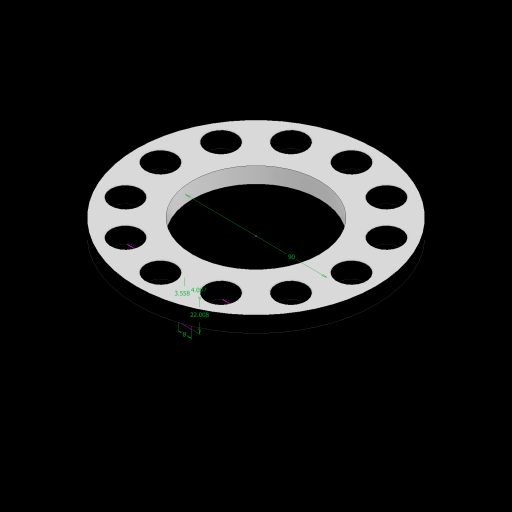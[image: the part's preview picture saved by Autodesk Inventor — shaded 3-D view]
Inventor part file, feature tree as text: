
AUTODESK INVENTOR PART (.ipt)
format: ipt  version: 2023 (Build 270158000, 158)  size: 1,133,056 bytes
history: native  units: mm
features: sketch x10, extrude x9, plane x2, fillet x1, projected_geometry x1
ambient origin geometry x8: Origin, YZ Plane, XZ Plane, XY Plane, X Axis, Y Axis, Z Axis, Center Point
bodies: Solid1 (feature_tree)
feature tree (23):
  extrude  "Extrusion1"  Depth=120.0mm
  extrude  "Extrusion2"  Depth=120.0mm TaperAngle=360.0deg
  extrude  "Extrusion9"  Depth=10.0mm
  extrude  "Extrusion10"  Depth=10.0mm TaperAngle=360.0deg
  extrude  "Extrusion11"  Depth=18.5mm
  extrude  "Extrusion12"  Depth=10.0mm TaperAngle=0.0deg
  extrude  "Extrusion13"  Depth=140.0mm TaperAngle=0.0deg
  fillet  "Fillet2"  Radius=10.0mm
  extrude  "Extrusion14"  Depth=10.0mm
  extrude  "Extrusion15"  Depth=10.0mm TaperAngle=0.0deg
  plane  "Work Plane2"
  sketch  "Sketch13"  dims[d110=10.0mm d111=0.0mm d112=10.0mm d113=0.0mm d114=8.0mm d115=3.558mm d116=4.097mm d117=22.008mm]
  plane  "Work Plane3"
  sketch  "Sketch1"  dims[d0=150.0mm d1=120.0mm]
  sketch  "Sketch2"  dims[d2=18.5mm d3=120.0mm d5=360.0deg]
  sketch  "Sketch3"  dims[d7=10.0mm d8=0.0mm d9=90.0mm]
  sketch  "Sketch7"  dims[d10=130.0mm d11=0.0mm d67=120.0mm d68=360.0deg d69=10.0mm d70=0.0mm]
  sketch  "Sketch8"  dims[d71=120.0mm d72=18.5mm]
  sketch  "Sketch9"  dims[d73=120.0mm d75=360.0deg d77=10.0mm d78=0.0mm]
  sketch  "Sketch10"  dims[d92=80.0mm d93=140.0mm d94=0.0mm]
  projected_geometry  "Projected Loop1"
  sketch  "Sketch11"  dims[d96=120.0mm d97=200.0mm d98=15.0deg d99=10.0mm d100=10.0mm d101=80.0mm d102=360.0deg d103=6.0mm d104=5.0mm d105=10.0mm d106=0.0mm]
  sketch  "Sketch12"  dims[d107=10.0mm d108=0.0mm d109=2.0mm]
